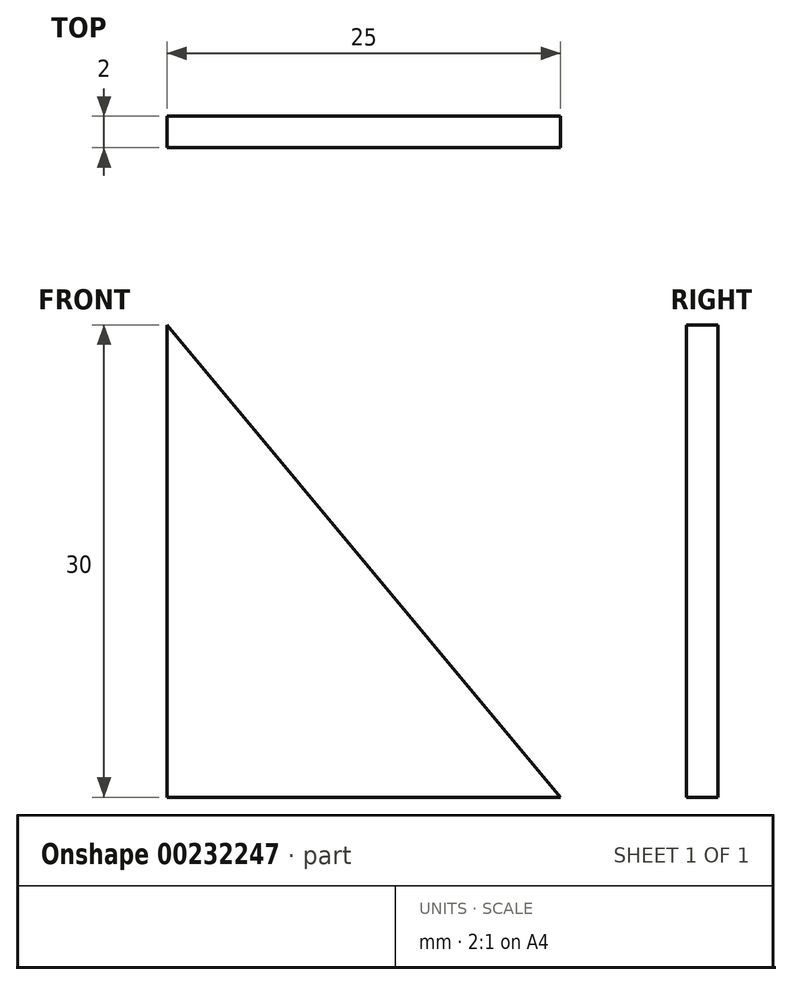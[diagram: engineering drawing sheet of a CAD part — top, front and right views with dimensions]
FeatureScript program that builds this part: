
annotation { "Feature Type Name" : "Feature", "Feature Type Description" : "" }
export const myFeature = defineFeature(function(context is Context, id is Id, definition is map)
    precondition{}
    {
        {
            var Q0;
            Q0=qCreatedBy(makeId("Front.planeOp"),FACE);
            var sketch = newSketch(context, id + "F0", { "sketchPlane" : qUnion([Q0])});
            skLineSegment(sketch, "E0.top", {"start": v(-22.3, -10.88) * mm, "end": v(2.7, -10.88) * mm});
            skLineSegment(sketch, "E0.left", {"start": v(-22.3, 19.12) * mm, "end": v(-22.3, -10.88) * mm});
            skLineSegment(sketch, "E1", {"start": v(-22.3, 19.12) * mm, "end": v(2.7, -10.88) * mm});
            skSolve(sketch);
        }
        {
            var Q0;
            Q0=makeQuery(id+"F0.imprint","IMPRINT",FACE,{"disambiguationData":[TD([[makeQuery(id+"F0.imprint","IMPRINT",EDGE,{"derivedFrom":sQuery(id+"F0.wireOp",EDGE,"E0.top")}),1.0]])]});
            extrude(context, id + "F1", {"entities" : qUnion([Q0]), "depth" : 2 * mm});
        }
    });
